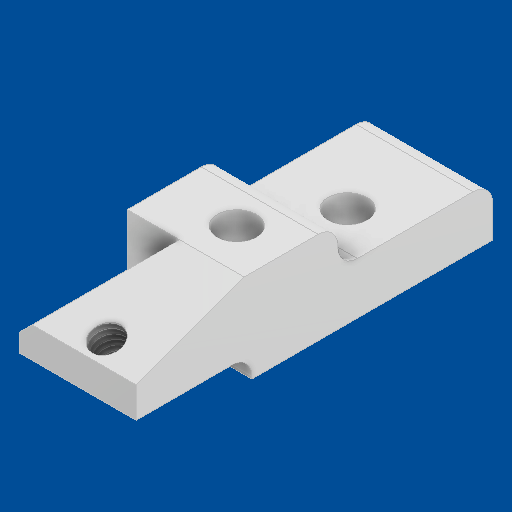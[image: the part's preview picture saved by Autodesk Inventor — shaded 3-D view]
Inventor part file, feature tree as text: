
AUTODESK INVENTOR PART (.ipt)
format: ipt  version: 2025 (Build 290162000, 162)  size: 243,712 bytes
history: native  units: in
note: dims shown in document units (in); Inventor stores cm internally (conversion verified against a paired STEP export)
features: move_body x12, direct_edit x9, sketch x2, hole x2, other x2, fillet x1
ambient origin geometry x8: Origin, YZ Plane, XZ Plane, XY Plane, X Axis, Y Axis, Z Axis, Center Point
bodies: Solid1 (feature_tree), Body10 (feature_tree)
feature tree (28):
  direct_edit  "Direct Edit1"
  direct_edit  "Direct Edit2"
  sketch  "Sketch1"  dims[d0=0.0in d1=0.0in d2=0.0254in d3=0.0394in]
  direct_edit  "Direct Edit3"
  hole  "Hole1"  [1 undecoded]
  hole  "Hole2"  [1 undecoded]
  fillet  "Fillet1"  [1 undecoded]
  direct_edit  "Direct Edit4"
  direct_edit  "Direct Edit5"
  direct_edit  "Direct Edit6"
  direct_edit  "Direct Edit7"
  direct_edit  "Direct Edit8"
  direct_edit  "Direct Edit9"
  sketch  "Sketch2"  dims[d4=0.0394in d5=0.0968in d6=2.3622in d7=0.1575in d8=0.0787in d9=90.0deg d10=3.1811in d11=0.8108in d12=0.0968in d13=2.3622in d14=0.1575in d15=0.0787in d16=90.0deg d17=3.1811in d18=0.8108in d19=0.063in d20=0.0in d21=0.0in d22=-0.0008in d23=0.0in d24=0.0in d25=-0.0035in d26=0.0in d27=0.0in d28=-0.0047in d29=0.0in d30=0.0in d31=-0.0047in d32=0.0in d33=0.0in d34=-0.0047in d36=0.0051in d37=-0.002in d38=0.0in d39=0.0in d40=0.0in d41=-0.0043in d42=0.0in d43=-0.0004in d44=0.0in d45=0.0in d46=-0.002in d47=0.0in d48=0.0in d49=0.0in d50=0.0in d51=-0.0008in d52=0.0in d53=0.0in d54=0.0008in]
  move_body  "Move1"
  other  "Size1"
  other  "Size2"
  move_body  "Move2"
  move_body  "Move3"
  move_body  "Move4"
  move_body  "Move5"
  move_body  "Move6"
  move_body  "Move7"
  move_body  "Move8"
  move_body  "Move9"
  move_body  "Move10"
  move_body  "Move11"
  move_body  "Move12"
note: 3 required parameter values undecoded (feature->parameter linkage not recoverable at this tier; creation-order binding heuristic only, values carry confidence <= 0.55)
